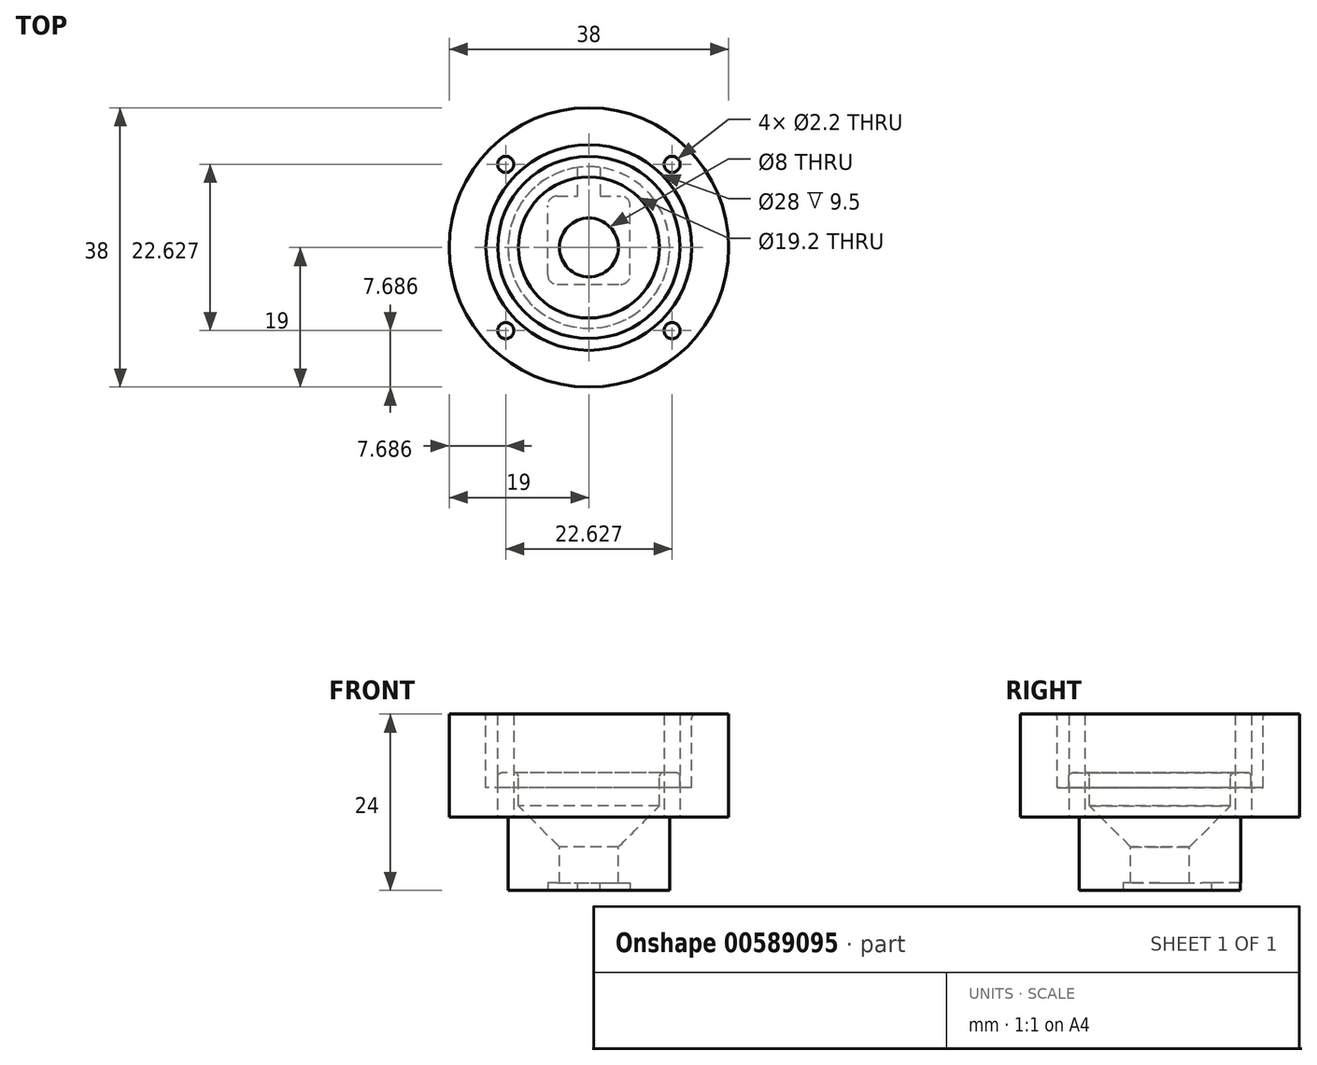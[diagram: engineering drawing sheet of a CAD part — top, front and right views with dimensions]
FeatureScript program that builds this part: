
annotation { "Feature Type Name" : "Feature", "Feature Type Description" : "" }
export const myFeature = defineFeature(function(context is Context, id is Id, definition is map)
    precondition{}
    {
        {
            var Q0;
            Q0=qCreatedBy(makeId("Front.planeOp"),FACE);
            var sketch = newSketch(context, id + "F0", { "sketchPlane" : qUnion([Q0])});
            skLineSegment(sketch, "E0", {"start": v(-14, 9.5) * mm, "end": v(-14, 0) * mm});
            skLineSegment(sketch, "E1", {"start": v(-4, -14) * mm, "end": v(-11, -14) * mm});
            skLineSegment(sketch, "E2", {"start": v(-19, 10) * mm, "end": v(-14.5, 10) * mm});
            skLineSegment(sketch, "E3", {"start": v(-9.6, -2.5) * mm, "end": v(-9.6, 1.5) * mm});
            skLineSegment(sketch, "E4", {"start": v(-12.4, 0) * mm, "end": v(-14, 0) * mm});
            skLineSegment(sketch, "E5", {"start": v(-9.6, -2.5) * mm, "end": v(-4, -8.1) * mm});
            skLineSegment(sketch, "E6", {"start": v(-4, -8.1) * mm, "end": v(-4, -14) * mm});
            skPoint(sketch, "E7.visualSharp", {"position": v(-14, 10) * mm});
            skArc(sketch, "E7.filletArc", {"start": v(-14, 9.5) * mm, "mid": v(-14.15, 9.85) * mm, "end": v(-14.5, 10) * mm});
            skLineSegment(sketch, "E8", {"start": v(-12.4, 0) * mm, "end": v(-12.4, 1.5) * mm});
            skLineSegment(sketch, "E9", {"start": v(-11.9, 2) * mm, "end": v(-10.1, 2) * mm});
            skPoint(sketch, "E10.orphan", {"position": v(-9.6, 0) * mm});
            skPoint(sketch, "E11.visualSharp", {"position": v(-12.4, 2) * mm});
            skArc(sketch, "E11.filletArc", {"start": v(-11.9, 2) * mm, "mid": v(-12.25, 1.85) * mm, "end": v(-12.4, 1.5) * mm});
            skPoint(sketch, "E12.visualSharp", {"position": v(-9.6, 2) * mm});
            skArc(sketch, "E12.filletArc", {"start": v(-9.6, 1.5) * mm, "mid": v(-9.75, 1.85) * mm, "end": v(-10.1, 2) * mm});
            skLineSegment(sketch, "E13", {"start": v(-19, -4) * mm, "end": v(-19, 10) * mm});
            skLineSegment(sketch, "E14", {"start": v(0, 0) * mm, "end": v(0, -14) * mm, "construction": true});
            skLineSegment(sketch, "E15", {"start": v(-19, -4) * mm, "end": v(-11, -4) * mm});
            skLineSegment(sketch, "E16", {"start": v(-11, -4) * mm, "end": v(-11, -14) * mm});
            skSolve(sketch);
        }
        {
            var Q0;
            Q0 = qSketchRegion(id + "F0", true);
            var Q1;
            Q1=sQuery(id+"F0.wireOp",EDGE,"E14");
            revolve(context, id + "F1", {"entities" : qUnion([Q0]), "axis" : qUnion([Q1]), "revolveType" : RevolveType.FULL});
        }
        {
            var Q0;
            Q0=makeQuery(id+"F1.opRevolve","SWEPT_FACE",FACE,{"disambiguationData":[OSD([sQuery(id+"F0.wireOp",EDGE,"E15")])]});
            var sketch = newSketch(context, id + "F2", { "sketchPlane" : qUnion([Q0])});
            skCircle(sketch, "E17", {"center": v(11.31, 11.31) * mm, "radius": 1.1 * mm});
            skCircle(sketch, "E18", {"center": v(-11.31, -11.31) * mm, "radius": 1.1 * mm});
            skCircle(sketch, "E19", {"center": v(11.31, -11.31) * mm, "radius": 1.1 * mm});
            skCircle(sketch, "E20", {"center": v(-11.31, 11.31) * mm, "radius": 1.1 * mm});
            skCircle(sketch, "E21", {"center": v(0, 0) * mm, "radius": 16 * mm, "construction": true});
            skLineSegment(sketch, "E22", {"start": v(-11.31, 11.31) * mm, "end": v(11.31, -11.31) * mm, "construction": true});
            skLineSegment(sketch, "E23", {"start": v(11.31, 11.31) * mm, "end": v(-11.31, -11.31) * mm, "construction": true});
            skSolve(sketch);
        }
        {
            var Q0;
            Q0 = qSketchRegion(id + "F2", true);
            extrude(context, id + "F3", {"entities" : qUnion([Q0]), "operationType" : NewBodyOperationType.REMOVE, "endBound" : BoundingType.UP_TO_NEXT, "oppositeDirection" : true, "depth" : 25 * mm, "offsetDistance" : 25 * mm});
        }
        {
            var Q0;
            Q0=makeQuery(id+"F1.opRevolve","SWEPT_FACE",FACE,{"disambiguationData":[OSD([sQuery(id+"F0.wireOp",EDGE,"E1")])]});
            var sketch = newSketch(context, id + "F4", { "sketchPlane" : qUnion([Q0])});
            skLineSegment(sketch, "E24.bottom", {"start": v(-4.33, 5) * mm, "end": v(4.33, 5) * mm});
            skLineSegment(sketch, "E24.top", {"start": v(-4.33, -7) * mm, "end": v(-1.5, -7) * mm});
            skLineSegment(sketch, "E24.left", {"start": v(-5.6, 3.74) * mm, "end": v(-5.6, -5.72) * mm});
            skLineSegment(sketch, "E24.right", {"start": v(5.6, 3.74) * mm, "end": v(5.6, -5.72) * mm});
            skPoint(sketch, "E25.visualSharp", {"position": v(-5.6, 5) * mm});
            skArc(sketch, "E25.filletArc", {"start": v(-4.33, 5) * mm, "mid": v(-5.23, 4.64) * mm, "end": v(-5.6, 3.74) * mm});
            skPoint(sketch, "E26.visualSharp", {"position": v(5.6, 5) * mm});
            skArc(sketch, "E26.filletArc", {"start": v(5.6, 3.74) * mm, "mid": v(5.23, 4.64) * mm, "end": v(4.33, 5) * mm});
            skPoint(sketch, "E27.visualSharp", {"position": v(5.6, -7) * mm});
            skArc(sketch, "E27.filletArc", {"start": v(4.33, -7) * mm, "mid": v(5.23, -6.62) * mm, "end": v(5.6, -5.72) * mm});
            skPoint(sketch, "E28.visualSharp", {"position": v(-5.6, -7) * mm});
            skArc(sketch, "E28.filletArc", {"start": v(-5.6, -5.72) * mm, "mid": v(-5.23, -6.62) * mm, "end": v(-4.33, -6.99) * mm});
            skLineSegment(sketch, "E29", {"start": v(-1.5, -7) * mm, "end": v(-1.5, -12) * mm});
            skLineSegment(sketch, "E30", {"start": v(1.5, -12) * mm, "end": v(1.5, -7) * mm});
            skLineSegment(sketch, "E31.trimOffspring", {"start": v(1.5, -7) * mm, "end": v(4.33, -7) * mm});
            skArc(sketch, "E32", {"start": v(-1.5, -12) * mm, "mid": v(0, -13.5) * mm, "end": v(1.5, -12) * mm});
            skSolve(sketch);
        }
        {
            var Q0;
            Q0 = qSketchRegion(id + "F4", true);
            extrude(context, id + "F5", {"entities" : qUnion([Q0]), "operationType" : NewBodyOperationType.REMOVE, "oppositeDirection" : true, "depth" : 1 * mm, "offsetDistance" : 25 * mm});
        }
    });
